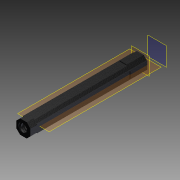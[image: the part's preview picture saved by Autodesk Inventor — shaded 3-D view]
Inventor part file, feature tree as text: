
AUTODESK INVENTOR PART (.ipt)
format: ipt  version: 2012 (Build 160160000, 160)  size: 2,129,408 bytes
history: native  units: in
note: dims shown in document units (in); Inventor stores cm internally (conversion verified against a paired STEP export)
features: reference x10, sketch x9, extrude x7, plane x3, projected_geometry x2, helix x1, fillet x1
ambient origin geometry x8: Origin, YZ Plane, XZ Plane, XY Plane, X Axis, Y Axis, Z Axis, Center Point
feature tree (33):
  plane  "Work Plane1"
  plane  "Work Plane2"
  extrude  "Extrusion7"  Depth=6.8898in TaperAngle=0.0deg
  sketch  "Sketch12"  dims[d48=1.0in d49=5.0in d50=0.0in d53=0.3937in d118=0.7559in]
  extrude  "Extrusion9"  Depth=0.3937in
  sketch  "Sketch16"  dims[d138=0.2362in d139=0.3937in d140=12.5984in d141=0.0in d142=90.0deg d143=90.0deg d144=0.0in d145=0.0in d152=0.0118in]
  plane  "Work Plane3"
  sketch  "Sketch17"  dims[d153=0.0118in d154=0.0118in]
  helix  "Coil8"  [1 undecoded]
  extrude  "Extrusion12"  Depth=0.1417in
  fillet  "Fillet10"  Radius=0.0906in
  extrude  "Extrusion15"  Depth=0.0118in
  extrude  "Extrusion16"  Depth=0.0118in
  extrude  "Extrusion17"  Depth=0.0118in
  extrude  "Extrusion18"  Depth=0.0118in
  sketch  "Sketch11"  dims[d0=0.04in d40=6.8898in d41=0.0in]
  reference  "Reference35"
  reference  "Reference36"
  reference  "Reference37"
  reference  "Reference38"
  sketch  "Sketch13"  dims[d119=0.7559in d122=0.1417in d131=0.0906in]
  reference  "Reference43"
  sketch  "Sketch20"  dims[d155=0.0118in d156=0.0118in]
  reference  "Reference44"
  sketch  "Sketch23"  dims[d157=0.0118in d158=0.0118in]
  reference  "Reference46"
  sketch  "Sketch24"  dims[d159=0.0118in]
  reference  "Reference47"
  reference  "Reference48"
  reference  "Reference49"
  sketch  "Sketch25"  dims[d163=0.0394in d164=0.0023in d165=0.0118in d166=0.0in d171=0.0394in d176=0.0118in d177=0.0118in d178=0.0in d179=0.0157in d180=0.0157in d181=0.3937in d182=0.0in d183=1.0in d184=0.0in d185=0.3937in d186=0.0in d188=0.0118in]
  projected_geometry  "Projected Loop6"
  projected_geometry  "Projected Loop7"
note: 1 required parameter value undecoded (feature->parameter linkage not recoverable at this tier; creation-order binding heuristic only, values carry confidence <= 0.55)
